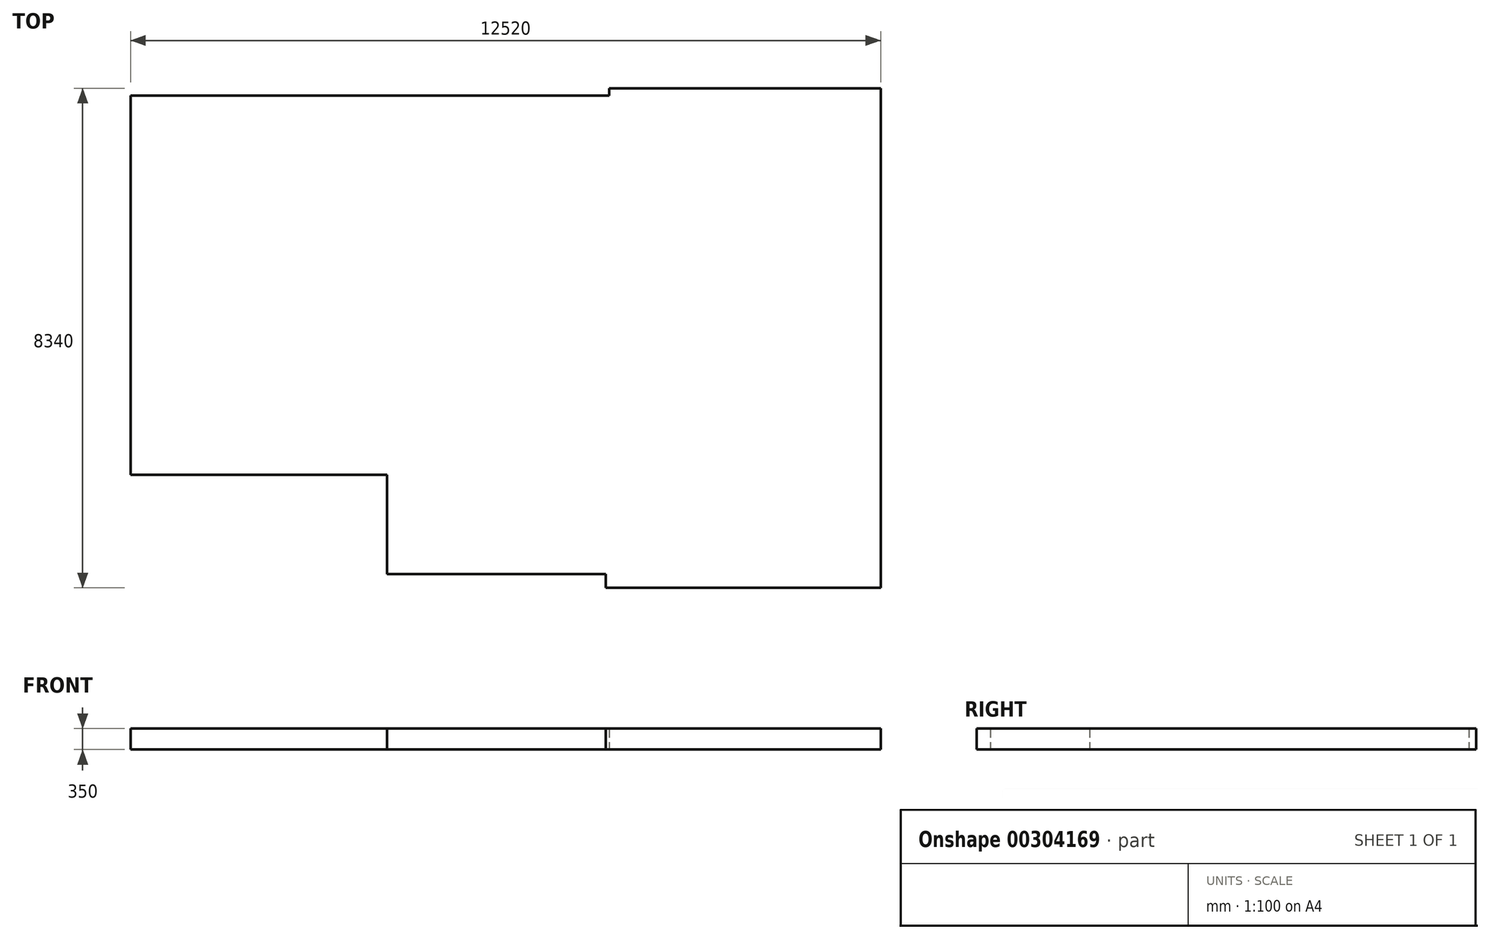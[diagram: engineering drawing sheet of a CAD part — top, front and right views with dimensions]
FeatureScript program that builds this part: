
annotation { "Feature Type Name" : "Feature", "Feature Type Description" : "" }
export const myFeature = defineFeature(function(context is Context, id is Id, definition is map)
    precondition{}
    {
        {
            var Q0;
            Q0=qCreatedBy(makeId("Top.planeOp"),FACE);
            var sketch = newSketch(context, id + "F0", { "sketchPlane" : qUnion([Q0])});
            skLineSegment(sketch, "E0", {"start": v(5088.43, 4492.55) * mm, "end": v(5088.43, -3847.45) * mm});
            skLineSegment(sketch, "E1", {"start": v(5088.43, -3847.45) * mm, "end": v(498.43, -3847.45) * mm});
            skLineSegment(sketch, "E2", {"start": v(498.43, -3847.45) * mm, "end": v(498.43, -3617.45) * mm});
            skLineSegment(sketch, "E3", {"start": v(498.43, -3617.45) * mm, "end": v(-3151.57, -3617.45) * mm});
            skLineSegment(sketch, "E4", {"start": v(-3151.57, -3617.45) * mm, "end": v(-3151.57, -1957.45) * mm});
            skLineSegment(sketch, "E5", {"start": v(-3151.57, -1957.45) * mm, "end": v(-7431.57, -1957.45) * mm});
            skLineSegment(sketch, "E6", {"start": v(-7431.57, -1957.45) * mm, "end": v(-7431.57, 4372.55) * mm});
            skLineSegment(sketch, "E7", {"start": v(-7431.57, 4372.55) * mm, "end": v(558.43, 4372.55) * mm});
            skLineSegment(sketch, "E8", {"start": v(558.43, 4372.55) * mm, "end": v(558.43, 4492.55) * mm});
            skLineSegment(sketch, "E9", {"start": v(558.43, 4492.55) * mm, "end": v(5088.43, 4492.55) * mm});
            skSolve(sketch);
        }
        {
            var Q0;
            Q0=makeQuery(id+"F0.imprint","IMPRINT",FACE,{"disambiguationData":[TD([[makeQuery(id+"F0.imprint","IMPRINT",EDGE,{"derivedFrom":sQuery(id+"F0.wireOp",EDGE,"E0")}),-1.0]])]});
            extrude(context, id + "F1", {"entities" : qUnion([Q0]), "depth" : 350 * mm});
        }
    });
